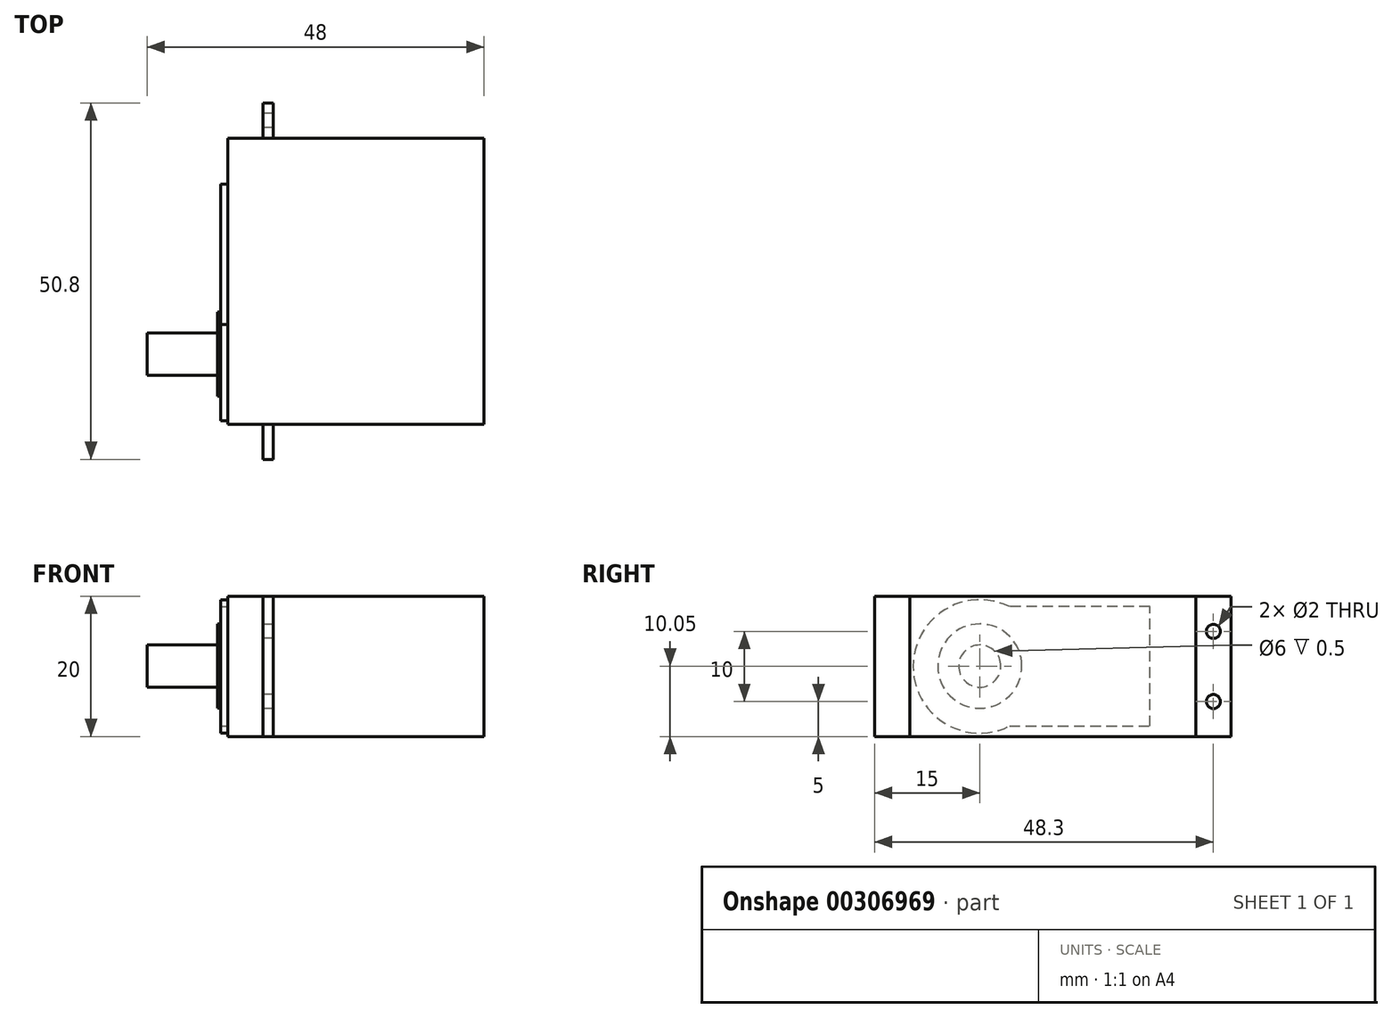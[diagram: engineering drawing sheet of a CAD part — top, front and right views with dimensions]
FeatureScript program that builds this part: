
annotation { "Feature Type Name" : "Feature", "Feature Type Description" : "" }
export const myFeature = defineFeature(function(context is Context, id is Id, definition is map)
    precondition{}
    {
        {
            var Q0;
            Q0=qCreatedBy(makeId("Front.planeOp"),FACE);
            var sketch = newSketch(context, id + "F0", { "sketchPlane" : qUnion([Q0])});
            skLineSegment(sketch, "E0.bottom", {"start": v(0, 0) * mm, "end": v(36.5, 0) * mm});
            skLineSegment(sketch, "E0.top", {"start": v(0, 20) * mm, "end": v(36.5, 20) * mm});
            skLineSegment(sketch, "E0.left", {"start": v(0, 0) * mm, "end": v(0, 20) * mm});
            skLineSegment(sketch, "E0.right", {"start": v(36.5, 0) * mm, "end": v(36.5, 20) * mm});
            skSolve(sketch);
        }
        {
            var Q0;
            Q0 = qSketchRegion(id + "F0", true);
            extrude(context, id + "F1", {"entities" : qUnion([Q0]), "endBound" : BoundingType.SYMMETRIC, "depth" : 40.8 * mm});
        }
        {
            var Q0;
            Q0=qCreatedBy(makeId("Right.planeOp"),FACE);
            cPlane(context, id + "F2", {"entities" : qUnion([Q0]), "cplaneType" : CPlaneType.OFFSET, "offset" : 5 * mm, "width" : 150 * mm, "height" : 150 * mm});
        }
        {
            var Q0;
            Q0=qCreatedBy(id+"F2.planeOp",FACE);
            var sketch = newSketch(context, id + "F3", { "sketchPlane" : qUnion([Q0])});
            skLineSegment(sketch, "E1.0", {"start": v(-20.4, 0) * mm, "end": v(-20.4, 20) * mm});
            skLineSegment(sketch, "E2", {"start": v(-20.4, 0) * mm, "end": v(-25.4, 0) * mm});
            skLineSegment(sketch, "E3", {"start": v(-25.4, 0) * mm, "end": v(-25.4, 20) * mm});
            skLineSegment(sketch, "E4", {"start": v(-25.4, 20) * mm, "end": v(-20.4, 20) * mm});
            skSolve(sketch);
        }
        {
            var Q0;
            Q0 = qSketchRegion(id + "F3", true);
            extrude(context, id + "F4", {"entities" : qUnion([Q0]), "depth" : 1.5 * mm});
        }
        {
            var Q0;
            Q0=makeQuery(id+"F4.opExtrude","SWEPT_BODY",BODY,{"disambiguationData":[OSD([sQuery(id+"F3.wireOp",EDGE,"E1.0"),sQuery(id+"F3.wireOp",EDGE,"E2"),sQuery(id+"F3.wireOp",EDGE,"E3"),sQuery(id+"F3.wireOp",EDGE,"E4")])]});
            var Q1;
            Q1=qCreatedBy(makeId("Front.planeOp"),FACE);
            mirror(context, id + "F5", {"entities" : qUnion([Q0]), "mirrorPlane" : qUnion([Q1])});
        }
        {
            var Q0;
            Q0=makeQuery(id+"F1.opExtrude","SWEPT_FACE",FACE,{"disambiguationData":[OSD([sQuery(id+"F0.wireOp",EDGE,"E0.left")])]});
            var sketch = newSketch(context, id + "F6", { "sketchPlane" : qUnion([Q0])});
            skArc(sketch, "E5", {"start": v(6.16, 1.5) * mm, "mid": v(19.9, 10) * mm, "end": v(6.16, 18.5) * mm});
            skPoint(sketch, "E5.centerSnap0", {"position": v(20.4, 10) * mm});
            skLineSegment(sketch, "E6", {"start": v(6.16, 1.5) * mm, "end": v(-13.84, 1.5) * mm});
            skLineSegment(sketch, "E7", {"start": v(-13.84, 1.5) * mm, "end": v(-13.84, 18.5) * mm});
            skLineSegment(sketch, "E8", {"start": v(-13.84, 18.5) * mm, "end": v(6.16, 18.5) * mm});
            skLineSegment(sketch, "E9", {"start": v(-45.44, 10) * mm, "end": v(35.03, 10) * mm, "construction": true});
            skPoint(sketch, "E9.startSnap0", {"position": v(-20.4, 10) * mm});
            skSolve(sketch);
        }
        {
            var Q0;
            Q0 = qSketchRegion(id + "F6", true);
            extrude(context, id + "F7", {"entities" : qUnion([Q0]), "operationType" : NewBodyOperationType.ADD, "depth" : 1 * mm});
        }
        {
            var Q0;
            Q0=makeQuery(id+"F7.opExtrude","CAP_FACE",FACE,{"disambiguationData":[OSD([sQuery(id+"F6.wireOp",EDGE,"E5"),sQuery(id+"F6.wireOp",EDGE,"E6"),sQuery(id+"F6.wireOp",EDGE,"E7"),sQuery(id+"F6.wireOp",EDGE,"E8")])],"isStart":false});
            var sketch = newSketch(context, id + "F8", { "sketchPlane" : qUnion([Q0])});
            skCircle(sketch, "E10", {"center": v(10.4, 10.05) * mm, "radius": 6 * mm});
            skPoint(sketch, "E11.0.3.start.orphan", {"position": v(-13.84, 1.5) * mm});
            skPoint(sketch, "E11.0.1.end.orphan", {"position": v(-13.84, 18.5) * mm});
            skPoint(sketch, "E11.0.0.end.orphan", {"position": v(6.16, 18.5) * mm});
            skPoint(sketch, "E11.0.0.start.orphan", {"position": v(6.16, 1.5) * mm});
            skSolve(sketch);
        }
        {
            var Q0;
            Q0 = qSketchRegion(id + "F8", true);
            extrude(context, id + "F9", {"entities" : qUnion([Q0]), "operationType" : NewBodyOperationType.ADD, "depth" : .5 * mm});
        }
        {
            var Q0;
            Q0=makeQuery(id+"F9.opExtrude","CAP_FACE",FACE,{"disambiguationData":[OSD([sQuery(id+"F8.wireOp",EDGE,"E10")])],"isStart":false});
            var sketch = newSketch(context, id + "F10", { "sketchPlane" : qUnion([Q0])});
            skCircle(sketch, "E12", {"center": v(10.4, 10.05) * mm, "radius": 3 * mm});
            skSolve(sketch);
        }
        {
            var Q0;
            Q0 = qSketchRegion(id + "F10", true);
            extrude(context, id + "F11", {"entities" : qUnion([Q0]), "operationType" : NewBodyOperationType.REMOVE, "oppositeDirection" : true, "depth" : .5 * mm});
        }
        {
            var Q0;
            Q0=makeQuery(id+"F9.opExtrude","CAP_FACE",FACE,{"disambiguationData":[OSD([sQuery(id+"F8.wireOp",EDGE,"E10")])],"isStart":false});
            var sketch = newSketch(context, id + "F12", { "sketchPlane" : qUnion([Q0])});
            skCircle(sketch, "E13.0", {"center": v(10.4, 10.05) * mm, "radius": 3 * mm});
            skSolve(sketch);
        }
        {
            var Q0;
            Q0 = qSketchRegion(id + "F12", true);
            extrude(context, id + "F13", {"entities" : qUnion([Q0]), "depth" : 10 * mm});
        }
        {
            var Q0;
            Q0=makeQuery(id+"F5.opPattern","COPY",FACE,{"derivedFrom":makeQuery(id+"F4.opExtrude","CAP_FACE",FACE,{"disambiguationData":[OSD([sQuery(id+"F3.wireOp",EDGE,"E1.0"),sQuery(id+"F3.wireOp",EDGE,"E2"),sQuery(id+"F3.wireOp",EDGE,"E3"),sQuery(id+"F3.wireOp",EDGE,"E4")])],"isStart":true}),"instanceName":"1"});
            var sketch = newSketch(context, id + "F14", { "sketchPlane" : qUnion([Q0])});
            skCircle(sketch, "E14", {"center": v(-22.9, 5) * mm, "radius": 1 * mm});
            skPoint(sketch, "E14.centerSnap0", {"position": v(-22.9, 0) * mm});
            skCircle(sketch, "E15", {"center": v(-22.9, 15) * mm, "radius": 1 * mm});
            skPoint(sketch, "E15.centerSnap0", {"position": v(-22.9, 20) * mm});
            skSolve(sketch);
        }
        {
            var Q0;
            Q0 = qSketchRegion(id + "F14", true);
            extrude(context, id + "F15", {"entities" : qUnion([Q0]), "operationType" : NewBodyOperationType.REMOVE, "oppositeDirection" : true, "depth" : 25 * mm});
        }
    });
